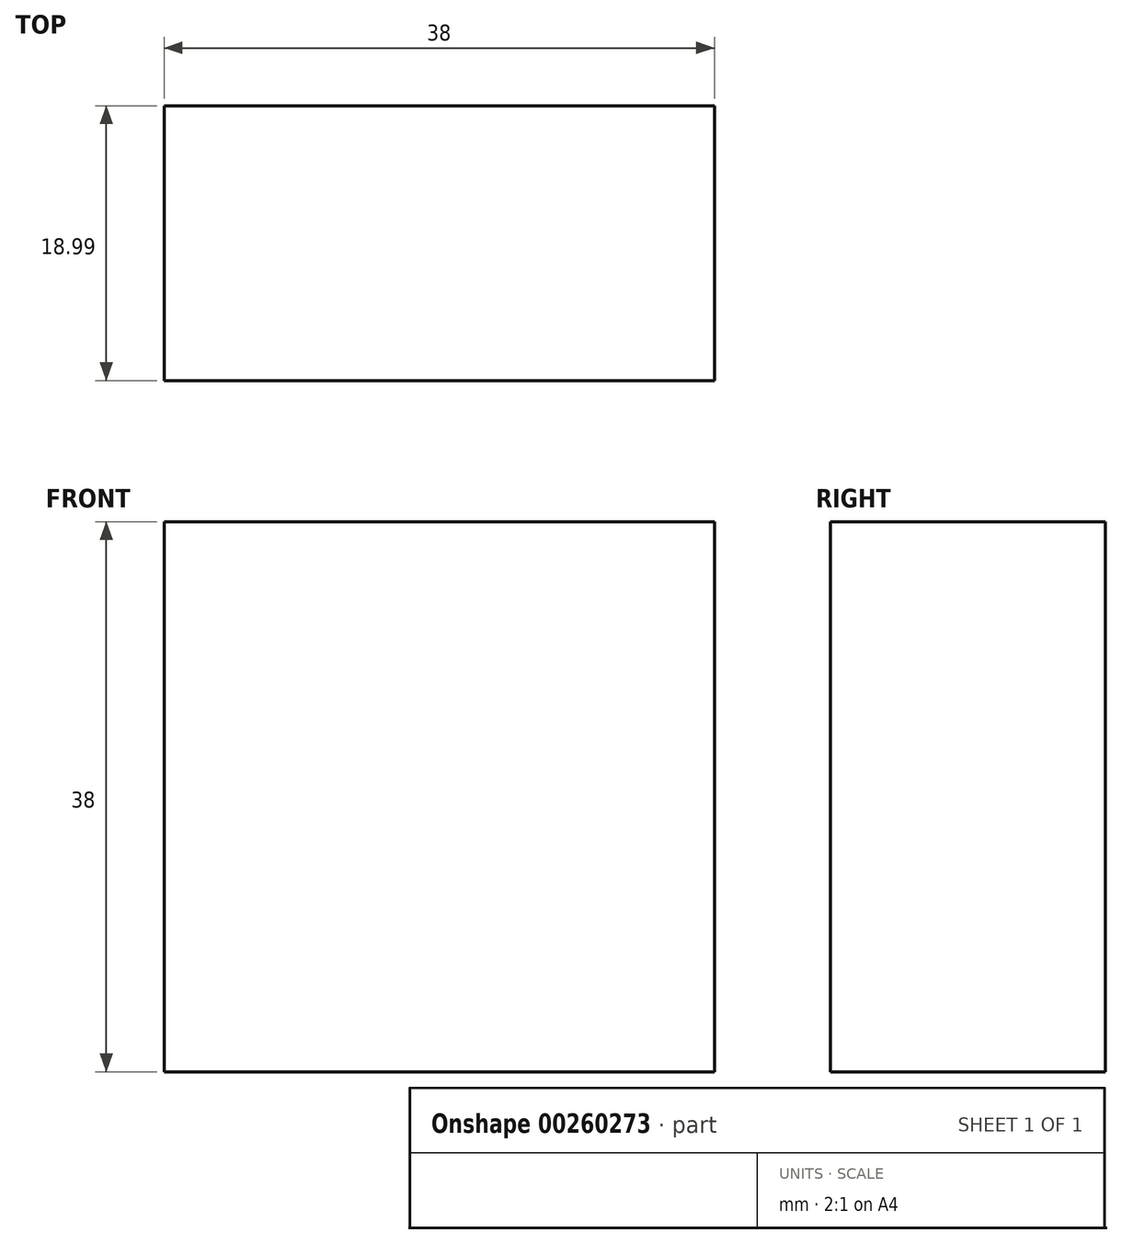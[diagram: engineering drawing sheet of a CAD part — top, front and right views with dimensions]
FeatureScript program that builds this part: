
annotation { "Feature Type Name" : "Feature", "Feature Type Description" : "" }
export const myFeature = defineFeature(function(context is Context, id is Id, definition is map)
    precondition{}
    {
        {
            var Q0;
            Q0=qCreatedBy(makeId("Front.planeOp"),FACE);
            var sketch = newSketch(context, id + "F0", { "sketchPlane" : qUnion([Q0])});
            skLineSegment(sketch, "E0.bottom", {"start": v(-18.99, 18.99) * mm, "end": v(19.01, 18.99) * mm});
            skLineSegment(sketch, "E0.top", {"start": v(-18.99, -19.01) * mm, "end": v(19.01, -19.01) * mm});
            skLineSegment(sketch, "E0.left", {"start": v(-18.99, 18.99) * mm, "end": v(-18.99, -19.01) * mm});
            skLineSegment(sketch, "E0.right", {"start": v(19.01, 18.99) * mm, "end": v(19.01, -19.01) * mm});
            skLineSegment(sketch, "E1", {"start": v(0.01, 18.99) * mm, "end": v(0, 0) * mm});
            skLineSegment(sketch, "E2", {"start": v(0, 0) * mm, "end": v(0.01, -19.01) * mm});
            skLineSegment(sketch, "E3", {"start": v(19.01, -0.01) * mm, "end": v(0, 0) * mm});
            skLineSegment(sketch, "E4", {"start": v(-18.99, -0.01) * mm, "end": v(0, 0) * mm});
            skSolve(sketch);
        }
        {
            var Q0;
            Q0 = qSketchRegion(id + "F0", true);
            extrude(context, id + "F1", {"entities" : qUnion([Q0]), "depth" : 18.99 * mm});
        }
    });
